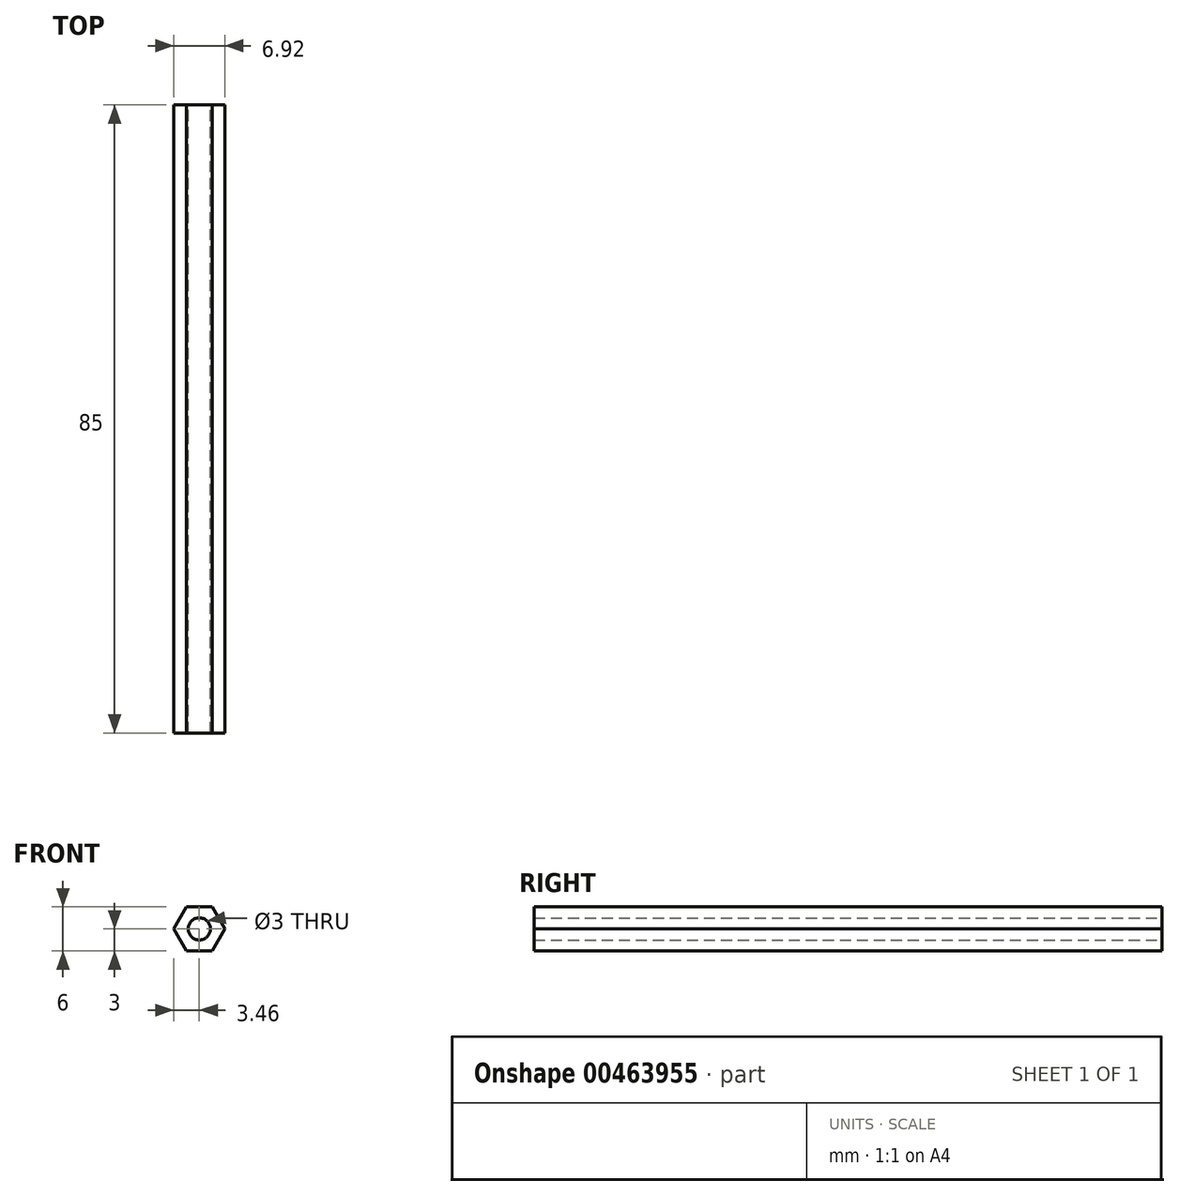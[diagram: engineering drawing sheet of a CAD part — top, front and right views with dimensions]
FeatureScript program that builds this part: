
annotation { "Feature Type Name" : "Feature", "Feature Type Description" : "" }
export const myFeature = defineFeature(function(context is Context, id is Id, definition is map)
    precondition{}
    {
        {
            var Q0;
            Q0=qCreatedBy(makeId("Front.planeOp"),FACE);
            var sketch = newSketch(context, id + "F0", { "sketchPlane" : qUnion([Q0])});
            skCircle(sketch, "E0.cCircle", {"center": v(0, 3) * mm, "radius": 3 * mm, "construction": true});
            skLineSegment(sketch, "E0.0", {"start": v(1.73, 6) * mm, "end": v(3.46, 3) * mm});
            skLineSegment(sketch, "E0.1", {"start": v(3.46, 3) * mm, "end": v(1.73, 0) * mm});
            skLineSegment(sketch, "E0.2", {"start": v(1.73, 0) * mm, "end": v(-1.73, 0) * mm});
            skLineSegment(sketch, "E0.3", {"start": v(-1.73, 0) * mm, "end": v(-3.46, 3) * mm});
            skLineSegment(sketch, "E0.4", {"start": v(-3.46, 3) * mm, "end": v(-1.73, 6) * mm});
            skLineSegment(sketch, "E0.5", {"start": v(-1.73, 6) * mm, "end": v(1.73, 6) * mm});
            skPoint(sketch, "E0.0.midPoint", {"position": v(2.6, 4.5) * mm});
            skPoint(sketch, "E1", {"position": v(0, 0) * mm});
            skCircle(sketch, "E2", {"center": v(0, 3) * mm, "radius": 1.5 * mm});
            skSolve(sketch);
        }
        {
            assignVariable(context, id + "F1", {"name" : "BoltShaftLength", "anyValue" : 40});
        }
        {
            assignVariable(context, id + "F2", {"name" : "StandoffLength", "anyValue" : (2 * getVariable(context, 'BoltShaftLength')) + 5});
        }
        {
            var Q0;
            Q0=makeQuery(id+"F0.imprint","IMPRINT",FACE,{"disambiguationData":[TD([[makeQuery(id+"F0.imprint","IMPRINT",EDGE,{"derivedFrom":sQuery(id+"F0.wireOp",EDGE,"E0.0")}),-1.0]])]});
            extrude(context, id + "F3", {"entities" : qUnion([Q0]), "endBound" : BoundingType.SYMMETRIC, "depth" : (getVariable(context, 'StandoffLength')) * mm});
        }
    });
